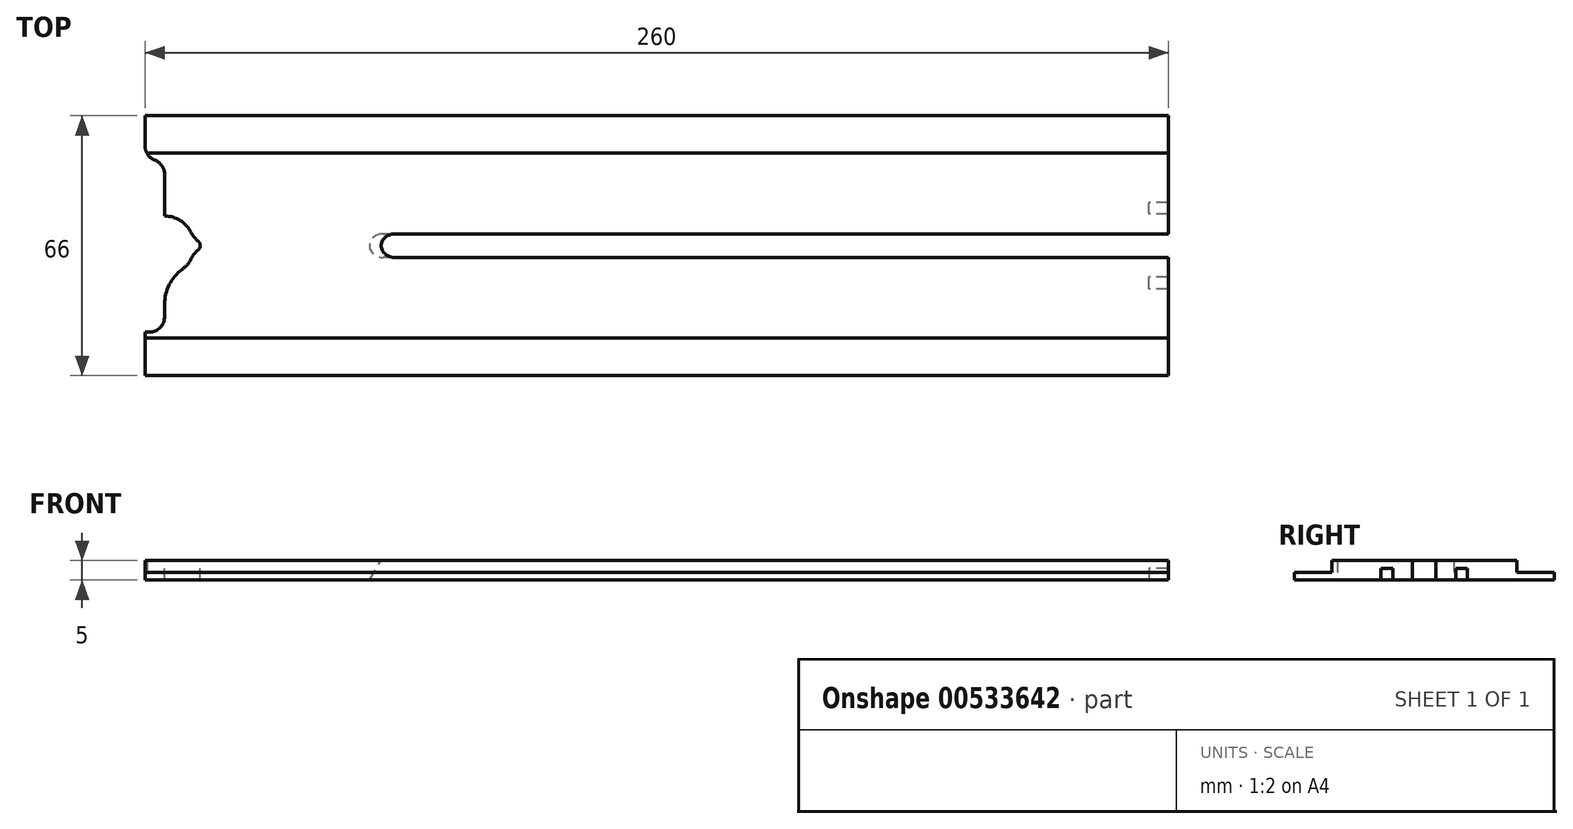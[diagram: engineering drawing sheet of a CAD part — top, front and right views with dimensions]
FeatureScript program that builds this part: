
annotation { "Feature Type Name" : "Feature", "Feature Type Description" : "" }
export const myFeature = defineFeature(function(context is Context, id is Id, definition is map)
    precondition{}
    {
        {
            var Q0;
            Q0=qCreatedBy(makeId("Top.planeOp"),FACE);
            var sketch = newSketch(context, id + "F0", { "sketchPlane" : qUnion([Q0])});
            skLineSegment(sketch, "E0.bottom", {"start": v(-61.94, 24.83) * mm, "end": v(198.06, 24.83) * mm});
            skLineSegment(sketch, "E0.top", {"start": v(-61.94, -41.17) * mm, "end": v(198.06, -41.17) * mm});
            skLineSegment(sketch, "E0.left", {"start": v(-61.94, 24.83) * mm, "end": v(-61.94, -41.17) * mm});
            skLineSegment(sketch, "E0.right", {"start": v(198.06, 24.83) * mm, "end": v(198.06, -41.17) * mm});
            skSolve(sketch);
        }
        {
            var Q0;
            Q0=makeQuery(id+"F0.imprint","IMPRINT",FACE,{"disambiguationData":[TD([[makeQuery(id+"F0.imprint","IMPRINT",EDGE,{"derivedFrom":sQuery(id+"F0.wireOp",EDGE,"E0.bottom")}),-1.0]])]});
            extrude(context, id + "F1", {"entities" : qUnion([Q0]), "depth" : 2 * mm, "offsetDistance" : 25 * mm});
        }
        {
            var Q0;
            Q0=makeQuery(id+"F1.opExtrude","CAP_FACE",FACE,{"disambiguationData":[OSD([sQuery(id+"F0.wireOp",EDGE,"E0.bottom"),sQuery(id+"F0.wireOp",EDGE,"E0.top"),sQuery(id+"F0.wireOp",EDGE,"E0.left"),sQuery(id+"F0.wireOp",EDGE,"E0.right")])],"isStart":false});
            var sketch = newSketch(context, id + "F2", { "sketchPlane" : qUnion([Q0])});
            skLineSegment(sketch, "E1.bottom", {"start": v(-61.94, 15.33) * mm, "end": v(198.06, 15.33) * mm});
            skLineSegment(sketch, "E1.top", {"start": v(-61.94, -31.67) * mm, "end": v(198.06, -31.67) * mm});
            skLineSegment(sketch, "E1.left", {"start": v(-61.94, 15.33) * mm, "end": v(-61.94, -31.67) * mm});
            skLineSegment(sketch, "E1.right", {"start": v(198.06, 15.33) * mm, "end": v(198.06, -31.67) * mm});
            skSolve(sketch);
        }
        {
            var Q0;
            Q0 = qSketchRegion(id + "F2", true);
            extrude(context, id + "F3", {"entities" : qUnion([Q0]), "operationType" : NewBodyOperationType.ADD, "depth" : 3 * mm, "offsetDistance" : 25 * mm});
        }
        {
            var Q0;
            Q0=makeQuery(id+"F3.opExtrude","CAP_FACE",FACE,{"disambiguationData":[OSD([sQuery(id+"F2.wireOp",EDGE,"E1.bottom"),sQuery(id+"F2.wireOp",EDGE,"E1.top"),sQuery(id+"F2.wireOp",EDGE,"E1.left"),sQuery(id+"F2.wireOp",EDGE,"E1.right")])],"isStart":false});
            var sketch = newSketch(context, id + "F4", { "sketchPlane" : qUnion([Q0])});
            skLineSegment(sketch, "E2", {"start": v(198.06, -8.17) * mm, "end": v(-61.94, -8.17) * mm, "construction": true});
            skLineSegment(sketch, "E3.bottom", {"start": v(198.06, -5.17) * mm, "end": v(-1.94, -5.17) * mm});
            skLineSegment(sketch, "E3.top", {"start": v(198.06, -11.17) * mm, "end": v(-1.94, -11.17) * mm});
            skLineSegment(sketch, "E3.left", {"start": v(198.06, -5.17) * mm, "end": v(198.06, -11.17) * mm});
            skLineSegment(sketch, "E3.right", {"start": v(-1.94, -5.17) * mm, "end": v(-1.94, -11.17) * mm});
            skPoint(sketch, "E4", {"position": v(-1.94, -8.17) * mm});
            skSolve(sketch);
        }
        {
            var Q0;
            Q0 = qSketchRegion(id + "F4", true);
            extrude(context, id + "F5", {"entities" : qUnion([Q0]), "operationType" : NewBodyOperationType.REMOVE, "oppositeDirection" : true, "depth" : 25 * mm, "offsetDistance" : 25 * mm});
        }
        {
            var Q0;
            Q0=makeQuery(id+"F5.boolean.opBoolean","INTERSECT",EDGE,{"derivedFrom":[makeQuery(id+"F1.opExtrude","CAP_FACE",FACE,{"disambiguationData":[OSD([sQuery(id+"F0.wireOp",EDGE,"E0.bottom"),sQuery(id+"F0.wireOp",EDGE,"E0.top"),sQuery(id+"F0.wireOp",EDGE,"E0.left"),sQuery(id+"F0.wireOp",EDGE,"E0.right")])],"isStart":true}),makeQuery(id+"F5.opExtrude","SWEPT_FACE",FACE,{"disambiguationData":[OSD([sQuery(id+"F4.wireOp",EDGE,"E3.right")])]})]});
            chamfer(context, id + "F6", {"entities" : qUnion([Q0]), "chamferType" : ChamferType.TWO_OFFSETS, "width1" : 3 * mm, "oppositeDirection" : false, "width2" : 5 * mm, "tangentPropagation" : true});
        }
        {
            var Q0;
            Q0=makeQuery(id+"F6.opChamfer","BLEND_EDGE",EDGE,{"blendedFrom":[makeQuery(id+"F5.boolean.opBoolean","INTERSECT",EDGE,{"derivedFrom":[makeQuery(id+"F1.opExtrude","CAP_FACE",FACE,{"disambiguationData":[OSD([sQuery(id+"F0.wireOp",EDGE,"E0.bottom"),sQuery(id+"F0.wireOp",EDGE,"E0.top"),sQuery(id+"F0.wireOp",EDGE,"E0.left"),sQuery(id+"F0.wireOp",EDGE,"E0.right")])],"isStart":true}),makeQuery(id+"F5.opExtrude","SWEPT_FACE",FACE,{"disambiguationData":[OSD([sQuery(id+"F4.wireOp",EDGE,"E3.right")])]})]}),makeQuery(id+"F5.boolean.opBoolean","COPY",FACE,{"derivedFrom":makeQuery(id+"F5.opExtrude","SWEPT_FACE",FACE,{"disambiguationData":[OSD([sQuery(id+"F4.wireOp",EDGE,"E3.top")])]})})],"blendedInto":[makeQuery(id+"F5.boolean.opBoolean","COPY",FACE,{"derivedFrom":makeQuery(id+"F5.opExtrude","SWEPT_FACE",FACE,{"disambiguationData":[OSD([sQuery(id+"F4.wireOp",EDGE,"E3.top")])]})})]});
            var Q1;
            Q1=makeQuery(id+"F6.opChamfer","BLEND_EDGE",EDGE,{"blendedFrom":[makeQuery(id+"F5.boolean.opBoolean","INTERSECT",EDGE,{"derivedFrom":[makeQuery(id+"F1.opExtrude","CAP_FACE",FACE,{"disambiguationData":[OSD([sQuery(id+"F0.wireOp",EDGE,"E0.bottom"),sQuery(id+"F0.wireOp",EDGE,"E0.top"),sQuery(id+"F0.wireOp",EDGE,"E0.left"),sQuery(id+"F0.wireOp",EDGE,"E0.right")])],"isStart":true}),makeQuery(id+"F5.opExtrude","SWEPT_FACE",FACE,{"disambiguationData":[OSD([sQuery(id+"F4.wireOp",EDGE,"E3.right")])]})]}),makeQuery(id+"F5.boolean.opBoolean","COPY",FACE,{"derivedFrom":makeQuery(id+"F5.opExtrude","SWEPT_FACE",FACE,{"disambiguationData":[OSD([sQuery(id+"F4.wireOp",EDGE,"E3.bottom")])]})})],"blendedInto":[makeQuery(id+"F5.boolean.opBoolean","COPY",FACE,{"derivedFrom":makeQuery(id+"F5.opExtrude","SWEPT_FACE",FACE,{"disambiguationData":[OSD([sQuery(id+"F4.wireOp",EDGE,"E3.bottom")])]})})]});
            fillet(context, id + "F7", {"entities" : qUnion([Q0, Q1]), "radius" : 3 * mm, "tangentPropagation" : true, "allowEdgeOverflow" : false});
        }
        {
            var Q0;
            Q0=makeQuery(id+"F1.opExtrude","CAP_FACE",FACE,{"disambiguationData":[OSD([sQuery(id+"F0.wireOp",EDGE,"E0.bottom"),sQuery(id+"F0.wireOp",EDGE,"E0.top"),sQuery(id+"F0.wireOp",EDGE,"E0.left"),sQuery(id+"F0.wireOp",EDGE,"E0.right")])],"isStart":true});
            var sketch = newSketch(context, id + "F8", { "sketchPlane" : qUnion([Q0])});
            skLineSegment(sketch, "E5.bottom", {"start": v(-61.94, 30.17) * mm, "end": v(-56.94, 30.17) * mm});
            skLineSegment(sketch, "E5.top", {"start": v(-61.94, -13.83) * mm, "end": v(-56.94, -13.83) * mm});
            skLineSegment(sketch, "E5.left", {"start": v(-61.94, 30.17) * mm, "end": v(-61.94, -13.83) * mm});
            skLineSegment(sketch, "E5.right", {"start": v(-56.94, 30.17) * mm, "end": v(-56.94, -13.83) * mm});
            skPoint(sketch, "E6", {"position": v(-61.94, 8.17) * mm});
            skSolve(sketch);
        }
        {
            var Q0;
            Q0=makeQuery(id+"F8.imprint","IMPRINT",FACE,{"disambiguationData":[TD([[makeQuery(id+"F8.imprint","IMPRINT",EDGE,{"derivedFrom":sQuery(id+"F8.wireOp",EDGE,"E5.bottom")}),-1.0]])]});
            extrude(context, id + "F9", {"entities" : qUnion([Q0]), "operationType" : NewBodyOperationType.REMOVE, "oppositeDirection" : true, "depth" : 25 * mm, "offsetDistance" : 25 * mm});
        }
        {
            var Q0;
            Q0=makeQuery(id+"F9.boolean.opBoolean","COPY",EDGE,{"derivedFrom":makeQuery(id+"F9.opExtrude","SWEPT_EDGE",EDGE,{"disambiguationData":[OSD([sQuery(id+"F8.wireOp",EDGE,"E5.bottom"),sQuery(id+"F8.wireOp",EDGE,"E5.right")])]})});
            var Q1;
            Q1=makeQuery(id+"F9.boolean.opBoolean","COPY",EDGE,{"derivedFrom":makeQuery(id+"F9.opExtrude","SWEPT_EDGE",EDGE,{"disambiguationData":[OSD([sQuery(id+"F8.wireOp",EDGE,"E5.top"),sQuery(id+"F8.wireOp",EDGE,"E5.right")])]})});
            fillet(context, id + "F10", {"entities" : qUnion([Q0, Q1]), "radius" : 4 * mm, "tangentPropagation" : true, "allowEdgeOverflow" : false});
        }
        {
            var Q0;
            Q0=makeQuery(id+"F1.opExtrude","CAP_FACE",FACE,{"disambiguationData":[OSD([sQuery(id+"F0.wireOp",EDGE,"E0.bottom"),sQuery(id+"F0.wireOp",EDGE,"E0.top"),sQuery(id+"F0.wireOp",EDGE,"E0.left"),sQuery(id+"F0.wireOp",EDGE,"E0.right")])],"isStart":true});
            var sketch = newSketch(context, id + "F11", { "sketchPlane" : qUnion([Q0])});
            skCircle(sketch, "E7", {"center": v(-56.94, 8.17) * mm, "radius": 7.5 * mm});
            skSolve(sketch);
        }
        {
            var Q0;
            {var subQ0=sQuery(id+"F11.wireOp",EDGE,"E7");var subQ1=makeQuery(id+"F9.boolean.opBoolean","COPY",EDGE,{"derivedFrom":makeQuery(id+"F9.opExtrude","CAP_EDGE",EDGE,{"disambiguationData":[OSD([sQuery(id+"F8.wireOp",EDGE,"E5.right")])],"isStart":true})});var subQ2=makeQuery(id+"F11.imprint","INTERSECT",VERTEX,{"disambiguationData":[OD(0.0)],"derivedFrom":[subQ1,subQ0]});Q0=makeQuery(id+"F11.imprint","IMPRINT",FACE,{"disambiguationData":[TD([[makeQuery(id+"F11.imprint","IMPRINT",EDGE,{"disambiguationData":[TD([[subQ2,1.0]])],"derivedFrom":subQ0}),1.0]])]});}
            extrude(context, id + "F12", {"entities" : qUnion([Q0]), "operationType" : NewBodyOperationType.REMOVE, "oppositeDirection" : true, "depth" : 25 * mm, "offsetDistance" : 25 * mm});
        }
        {
            var Q0;
            {var subQ0=sQuery(id+"F11.wireOp",EDGE,"E7");var subQ1=sQuery(id+"F8.wireOp",EDGE,"E5.right");Q0=makeQuery(id+"F12.boolean.opBoolean","COPY",EDGE,{"derivedFrom":makeQuery(id+"F12.opExtrude","SWEPT_EDGE",EDGE,{"disambiguationData":[OSD([subQ1,subQ0]),TDD([makeQuery(id+"F11.imprint","INTERSECT",VERTEX,{"disambiguationData":[OD(0.0)],"derivedFrom":[makeQuery(id+"F9.boolean.opBoolean","COPY",EDGE,{"derivedFrom":makeQuery(id+"F9.opExtrude","CAP_EDGE",EDGE,{"disambiguationData":[OSD([subQ1])],"isStart":true})}),subQ0]})])]})});}
            var Q1;
            {var subQ0=sQuery(id+"F11.wireOp",EDGE,"E7");var subQ1=sQuery(id+"F8.wireOp",EDGE,"E5.right");Q1=makeQuery(id+"F12.boolean.opBoolean","COPY",EDGE,{"derivedFrom":makeQuery(id+"F12.opExtrude","SWEPT_EDGE",EDGE,{"disambiguationData":[OSD([subQ1,subQ0]),TDD([makeQuery(id+"F11.imprint","INTERSECT",VERTEX,{"disambiguationData":[OD(1.0)],"derivedFrom":[makeQuery(id+"F9.boolean.opBoolean","COPY",EDGE,{"derivedFrom":makeQuery(id+"F9.opExtrude","CAP_EDGE",EDGE,{"disambiguationData":[OSD([subQ1])],"isStart":true})}),subQ0]})])]})});}
            fillet(context, id + "F13", {"entities" : qUnion([Q0, Q1]), "radius" : 11 * mm, "tangentPropagation" : true, "allowEdgeOverflow" : false});
        }
        {
            var Q0;
            Q0=makeQuery(id+"F1.opExtrude","CAP_FACE",FACE,{"disambiguationData":[OSD([sQuery(id+"F0.wireOp",EDGE,"E0.bottom"),sQuery(id+"F0.wireOp",EDGE,"E0.top"),sQuery(id+"F0.wireOp",EDGE,"E0.left"),sQuery(id+"F0.wireOp",EDGE,"E0.right")])],"isStart":true});
            var sketch = newSketch(context, id + "F14", { "sketchPlane" : qUnion([Q0])});
            skLineSegment(sketch, "E8.bottom", {"start": v(-41.33, 41.17) * mm, "end": v(198.06, 41.17) * mm});
            skLineSegment(sketch, "E8.top", {"start": v(-41.33, -24.83) * mm, "end": v(198.06, -24.83) * mm});
            skLineSegment(sketch, "E8.left", {"start": v(-41.33, 41.17) * mm, "end": v(-41.33, -24.83) * mm});
            skLineSegment(sketch, "E8.right", {"start": v(198.06, 41.17) * mm, "end": v(198.06, -24.83) * mm});
            skSolve(sketch);
        }
        {
            var Q0;
            Q0=makeQuery(id+"F1.opExtrude","CAP_FACE",FACE,{"disambiguationData":[OSD([sQuery(id+"F0.wireOp",EDGE,"E0.bottom"),sQuery(id+"F0.wireOp",EDGE,"E0.top"),sQuery(id+"F0.wireOp",EDGE,"E0.left"),sQuery(id+"F0.wireOp",EDGE,"E0.right")])],"isStart":true});
            var sketch = newSketch(context, id + "F15", { "sketchPlane" : qUnion([Q0])});
            skLineSegment(sketch, "E9.bottom", {"start": v(198.06, 19.17) * mm, "end": v(193.06, 19.17) * mm});
            skLineSegment(sketch, "E9.top", {"start": v(198.06, 16.17) * mm, "end": v(193.06, 16.17) * mm});
            skLineSegment(sketch, "E9.left", {"start": v(198.06, 19.17) * mm, "end": v(198.06, 16.17) * mm});
            skLineSegment(sketch, "E9.right", {"start": v(193.06, 19.17) * mm, "end": v(193.06, 16.17) * mm});
            skPoint(sketch, "E10", {"position": v(198.06, 17.67) * mm});
            skSolve(sketch);
        }
        {
            var Q0;
            Q0=makeQuery(id+"F15.imprint","IMPRINT",FACE,{"disambiguationData":[TD([[makeQuery(id+"F15.imprint","IMPRINT",EDGE,{"derivedFrom":sQuery(id+"F15.wireOp",EDGE,"E9.bottom")}),1.0]])]});
            extrude(context, id + "F16", {"entities" : qUnion([Q0]), "operationType" : NewBodyOperationType.REMOVE, "oppositeDirection" : true, "depth" : 3 * mm, "offsetDistance" : 25 * mm});
        }
        {
            var Q0;
            Q0=makeQuery(id+"F1.opExtrude","CAP_FACE",FACE,{"disambiguationData":[OSD([sQuery(id+"F0.wireOp",EDGE,"E0.bottom"),sQuery(id+"F0.wireOp",EDGE,"E0.top"),sQuery(id+"F0.wireOp",EDGE,"E0.left"),sQuery(id+"F0.wireOp",EDGE,"E0.right")])],"isStart":true});
            var sketch = newSketch(context, id + "F17", { "sketchPlane" : qUnion([Q0])});
            skLineSegment(sketch, "E11.bottom", {"start": v(198.06, 0.17) * mm, "end": v(193.06, 0.17) * mm});
            skLineSegment(sketch, "E11.top", {"start": v(198.06, -2.83) * mm, "end": v(193.06, -2.83) * mm});
            skLineSegment(sketch, "E11.left", {"start": v(198.06, 0.17) * mm, "end": v(198.06, -2.83) * mm});
            skLineSegment(sketch, "E11.right", {"start": v(193.06, 0.17) * mm, "end": v(193.06, -2.83) * mm});
            skSolve(sketch);
        }
        {
            var Q0;
            Q0=makeQuery(id+"F17.imprint","IMPRINT",FACE,{"disambiguationData":[TD([[makeQuery(id+"F17.imprint","IMPRINT",EDGE,{"derivedFrom":sQuery(id+"F17.wireOp",EDGE,"E11.bottom")}),1.0]])]});
            extrude(context, id + "F18", {"entities" : qUnion([Q0]), "operationType" : NewBodyOperationType.REMOVE, "oppositeDirection" : true, "depth" : 3 * mm, "offsetDistance" : 25 * mm});
        }
        {
            var Q0;
            Q0=makeQuery(id+"F9.boolean.opBoolean","COPY",EDGE,{"derivedFrom":makeQuery(id+"F9.opExtrude","SWEPT_EDGE",EDGE,{"disambiguationData":[OSD([sQuery(id+"F0.wireOp",EDGE,"E0.left"),sQuery(id+"F8.wireOp",EDGE,"E5.top"),sQuery(id+"F8.wireOp",EDGE,"E5.left")])]})});
            var Q1;
            Q1=makeQuery(id+"F9.boolean.opBoolean","COPY",EDGE,{"derivedFrom":makeQuery(id+"F9.opExtrude","SWEPT_EDGE",EDGE,{"disambiguationData":[OSD([sQuery(id+"F0.wireOp",EDGE,"E0.left"),sQuery(id+"F8.wireOp",EDGE,"E5.bottom"),sQuery(id+"F8.wireOp",EDGE,"E5.left")])]})});
            fillet(context, id + "F19", {"entities" : qUnion([Q0, Q1]), "radius" : 4 * mm, "tangentPropagation" : true, "allowEdgeOverflow" : false});
        }
        {
            var Q0;
            Q0=makeQuery(id+"F3.opExtrude","CAP_FACE",FACE,{"disambiguationData":[OSD([sQuery(id+"F2.wireOp",EDGE,"E1.bottom"),sQuery(id+"F2.wireOp",EDGE,"E1.top"),sQuery(id+"F2.wireOp",EDGE,"E1.left"),sQuery(id+"F2.wireOp",EDGE,"E1.right")])],"isStart":false});
            var sketch = newSketch(context, id + "F20", { "sketchPlane" : qUnion([Q0])});
            skCircle(sketch, "E12", {"center": v(-49.44, -8.17) * mm, "radius": 1.5 * mm});
            skSolve(sketch);
        }
        {
            var Q0;
            Q0 = qSketchRegion(id + "F20", true);
            extrude(context, id + "F21", {"entities" : qUnion([Q0]), "operationType" : NewBodyOperationType.REMOVE, "oppositeDirection" : true, "depth" : 25 * mm, "offsetDistance" : 25 * mm});
        }
        {
            var Q0;
            Q0=makeQuery(id+"F21.boolean.opBoolean","INTERSECT",EDGE,{"disambiguationData":[OD(0.0)],"derivedFrom":[makeQuery(id+"F12.boolean.opBoolean","COPY",FACE,{"derivedFrom":makeQuery(id+"F12.opExtrude","SWEPT_FACE",FACE,{"disambiguationData":[OSD([sQuery(id+"F11.wireOp",EDGE,"E7")])]})}),makeQuery(id+"F21.opExtrude","SWEPT_FACE",FACE,{"disambiguationData":[OSD([sQuery(id+"F20.wireOp",EDGE,"E12")])]})]});
            var Q1;
            Q1=makeQuery(id+"F21.boolean.opBoolean","INTERSECT",EDGE,{"disambiguationData":[OD(1.0)],"derivedFrom":[makeQuery(id+"F12.boolean.opBoolean","COPY",FACE,{"derivedFrom":makeQuery(id+"F12.opExtrude","SWEPT_FACE",FACE,{"disambiguationData":[OSD([sQuery(id+"F11.wireOp",EDGE,"E7")])]})}),makeQuery(id+"F21.opExtrude","SWEPT_FACE",FACE,{"disambiguationData":[OSD([sQuery(id+"F20.wireOp",EDGE,"E12")])]})]});
            fillet(context, id + "F22", {"entities" : qUnion([Q0, Q1]), "radius" : 6 * mm, "tangentPropagation" : true, "allowEdgeOverflow" : false});
        }
    });
